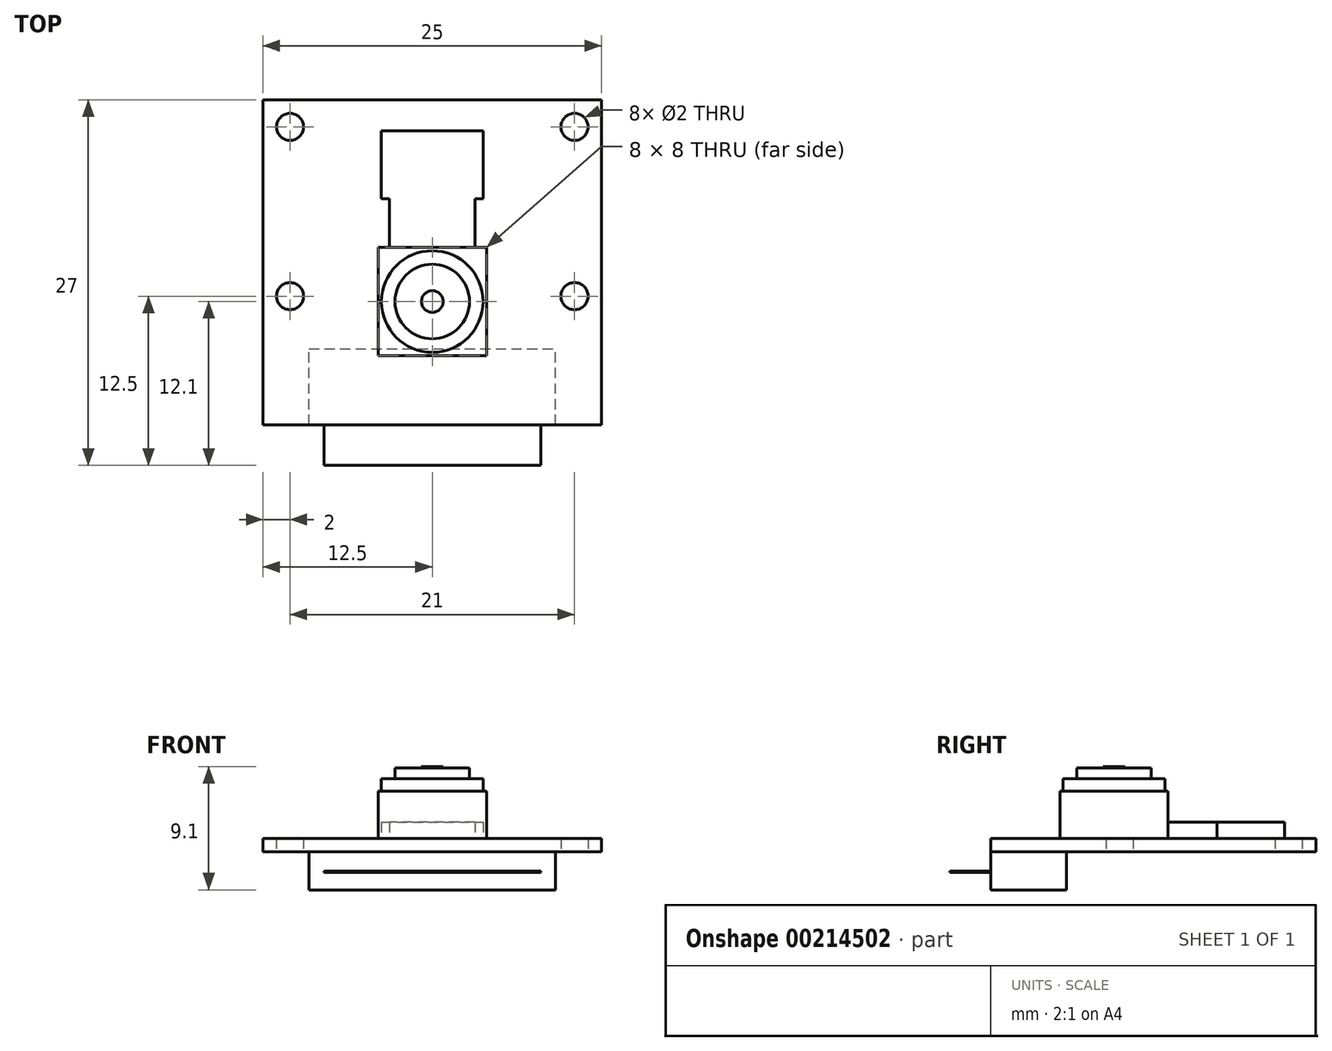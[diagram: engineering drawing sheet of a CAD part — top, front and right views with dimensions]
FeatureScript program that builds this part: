
annotation { "Feature Type Name" : "Feature", "Feature Type Description" : "" }
export const myFeature = defineFeature(function(context is Context, id is Id, definition is map)
    precondition{}
    {
        {
            var Q0;
            Q0=qCreatedBy(makeId("Top.planeOp"),FACE);
            var sketch = newSketch(context, id + "F0", { "sketchPlane" : qUnion([Q0])});
            skLineSegment(sketch, "E0.rect.bottom", {"start": v(12.5, 12) * mm, "end": v(-12.5, 12) * mm});
            skLineSegment(sketch, "E0.rect.top", {"start": v(12.5, -12) * mm, "end": v(-12.5, -12) * mm});
            skLineSegment(sketch, "E0.rect.left", {"start": v(12.5, 12) * mm, "end": v(12.5, -12) * mm});
            skLineSegment(sketch, "E0.rect.right", {"start": v(-12.5, 12) * mm, "end": v(-12.5, -12) * mm});
            skPoint(sketch, "E0.rect.middle", {"position": v(0, 0) * mm});
            skCircle(sketch, "E1", {"center": v(-10.5, 10) * mm, "radius": 1 * mm});
            skCircle(sketch, "E2", {"center": v(-10.5, -2.5) * mm, "radius": 1 * mm});
            skLineSegment(sketch, "E3", {"start": v(-10.5, 10) * mm, "end": v(-10.5, -12) * mm, "construction": true});
            skCircle(sketch, "E4.MirrorC", {"center": v(10.5, 10) * mm, "radius": 1 * mm});
            skCircle(sketch, "E5.MirrorC", {"center": v(10.5, -2.5) * mm, "radius": 1 * mm});
            skSolve(sketch);
        }
        {
            var Q0;
            Q0=makeQuery(id+"F0.imprint","IMPRINT",FACE,{"disambiguationData":[TD([[makeQuery(id+"F0.imprint","IMPRINT",EDGE,{"derivedFrom":sQuery(id+"F0.wireOp",EDGE,"E0.rect.bottom")}),1.0]])]});
            extrude(context, id + "F1", {"entities" : qUnion([Q0]), "depth" : 1 * mm});
        }
        {
            var Q0;
            Q0=makeQuery(id+"F1.opExtrude","CAP_FACE",FACE,{"disambiguationData":[OSD([sQuery(id+"F0.wireOp",EDGE,"E0.rect.bottom"),sQuery(id+"F0.wireOp",EDGE,"E0.rect.top"),sQuery(id+"F0.wireOp",EDGE,"E0.rect.left"),sQuery(id+"F0.wireOp",EDGE,"E0.rect.right"),sQuery(id+"F0.wireOp",EDGE,"E1"),sQuery(id+"F0.wireOp",EDGE,"E2"),sQuery(id+"F0.wireOp",EDGE,"E4.MirrorC"),sQuery(id+"F0.wireOp",EDGE,"E5.MirrorC")])],"isStart":false});
            var sketch = newSketch(context, id + "F2", { "sketchPlane" : qUnion([Q0])});
            skLineSegment(sketch, "E6", {"start": v(-12.5, -2.9) * mm, "end": v(12.5, -2.9) * mm, "construction": true});
            skLineSegment(sketch, "E7.rect.bottom", {"start": v(4, 1.1) * mm, "end": v(-4, 1.1) * mm});
            skLineSegment(sketch, "E7.rect.top", {"start": v(4, -6.9) * mm, "end": v(-4, -6.9) * mm});
            skLineSegment(sketch, "E7.rect.left", {"start": v(4, 1.1) * mm, "end": v(4, -6.9) * mm});
            skLineSegment(sketch, "E7.rect.right", {"start": v(-4, 1.1) * mm, "end": v(-4, -6.9) * mm});
            skPoint(sketch, "E7.rect.middle", {"position": v(0, -2.9) * mm});
            skCircle(sketch, "E8", {"center": v(0, -2.9) * mm, "radius": 3.75 * mm});
            skCircle(sketch, "E9", {"center": v(0, -2.9) * mm, "radius": 2.75 * mm});
            skLineSegment(sketch, "E10.bottom", {"start": v(-3.4, 1.1) * mm, "end": v(3.4, 1.1) * mm});
            skSolve(sketch);
        }
        {
            var Q0;
            Q0=qSketchRegion(id+"F2",true);
            var Q1;
            Q1=makeQuery(id+"F2.imprint","IMPRINT",FACE,{"disambiguationData":[TD([[makeQuery(id+"F2.imprint","IMPRINT",EDGE,{"derivedFrom":sQuery(id+"F2.wireOp",EDGE,"E8")}),1.0]])]});
            var Q2;
            Q2=makeQuery(id+"F2.imprint","IMPRINT",FACE,{"disambiguationData":[TD([[makeQuery(id+"F2.imprint","IMPRINT",EDGE,{"derivedFrom":sQuery(id+"F2.wireOp",EDGE,"E9")}),1.0]])]});
            extrude(context, id + "F3", {"entities" : qUnion([Q0, Q1, Q2]), "depth" : 3.5 * mm});
        }
        {
            var Q0;
            Q0=makeQuery(id+"F2.imprint","IMPRINT",FACE,{"disambiguationData":[TD([[makeQuery(id+"F2.imprint","IMPRINT",EDGE,{"derivedFrom":sQuery(id+"F2.wireOp",EDGE,"E8")}),1.0]])]});
            var Q1;
            Q1=makeQuery(id+"F2.imprint","IMPRINT",FACE,{"disambiguationData":[TD([[makeQuery(id+"F2.imprint","IMPRINT",EDGE,{"derivedFrom":sQuery(id+"F2.wireOp",EDGE,"E9")}),1.0]])]});
            extrude(context, id + "F4", {"entities" : qUnion([Q0, Q1]), "operationType" : NewBodyOperationType.ADD, "depth" : (3.5 + 0.9) * mm});
        }
        {
            var Q0;
            Q0=makeQuery(id+"F2.imprint","IMPRINT",FACE,{"disambiguationData":[TD([[makeQuery(id+"F2.imprint","IMPRINT",EDGE,{"derivedFrom":sQuery(id+"F2.wireOp",EDGE,"E9")}),1.0]])]});
            extrude(context, id + "F5", {"entities" : qUnion([Q0]), "operationType" : NewBodyOperationType.ADD, "depth" : 5.2 * mm});
        }
        {
            var Q0;
            Q0=makeQuery(id+"F5.opExtrude","CAP_FACE",FACE,{"disambiguationData":[OSD([sQuery(id+"F2.wireOp",EDGE,"E9")])],"isStart":false});
            var sketch = newSketch(context, id + "F6", { "sketchPlane" : qUnion([Q0])});
            skCircle(sketch, "E11", {"center": v(0, -2.9) * mm, "radius": 0.8 * mm});
            skSolve(sketch);
        }
        {
            var Q0;
            Q0=makeQuery(id+"F6.imprint","IMPRINT",FACE,{"disambiguationData":[TD([[makeQuery(id+"F6.imprint","IMPRINT",EDGE,{"derivedFrom":sQuery(id+"F6.wireOp",EDGE,"E11")}),1.0]])]});
            extrude(context, id + "F7", {"entities" : qUnion([Q0]), "depth" : 0.1 * mm});
        }
        {
            var Q0;
            Q0=makeQuery(id+"F1.opExtrude","CAP_FACE",FACE,{"disambiguationData":[OSD([sQuery(id+"F0.wireOp",EDGE,"E0.rect.bottom"),sQuery(id+"F0.wireOp",EDGE,"E0.rect.top"),sQuery(id+"F0.wireOp",EDGE,"E0.rect.left"),sQuery(id+"F0.wireOp",EDGE,"E0.rect.right"),sQuery(id+"F0.wireOp",EDGE,"E1"),sQuery(id+"F0.wireOp",EDGE,"E2"),sQuery(id+"F0.wireOp",EDGE,"E4.MirrorC"),sQuery(id+"F0.wireOp",EDGE,"E5.MirrorC")])],"isStart":true});
            var sketch = newSketch(context, id + "F8", { "sketchPlane" : qUnion([Q0])});
            skLineSegment(sketch, "E12.bottom", {"start": v(-9.1, 12) * mm, "end": v(9.1, 12) * mm});
            skLineSegment(sketch, "E12.top", {"start": v(-9.1, 6.4) * mm, "end": v(9.1, 6.4) * mm});
            skLineSegment(sketch, "E12.left", {"start": v(-9.1, 12) * mm, "end": v(-9.1, 6.4) * mm});
            skLineSegment(sketch, "E12.right", {"start": v(9.1, 12) * mm, "end": v(9.1, 6.4) * mm});
            skSolve(sketch);
        }
        {
            var Q0;
            Q0=qSketchRegion(id+"F8",true);
            extrude(context, id + "F9", {"entities" : qUnion([Q0]), "depth" : 2.8 * mm});
        }
        {
            var Q0;
            Q0=makeQuery(id+"F2.imprint","IMPRINT",FACE,{"disambiguationData":[TD([[makeQuery(id+"F2.imprint","IMPRINT",EDGE,{"derivedFrom":sQuery(id+"F2.wireOp",EDGE,"E7.rect.top")}),1.0]])]});
            var sketch = newSketch(context, id + "F10", { "sketchPlane" : qUnion([Q0])});
            skLineSegment(sketch, "E13.bottom", {"start": v(-3.75, 1.1) * mm, "end": v(3.75, 1.1) * mm});
            skLineSegment(sketch, "E13.top", {"start": v(-3.75, 9.7) * mm, "end": v(3.75, 9.7) * mm});
            skLineSegment(sketch, "E13.left", {"start": v(-3.75, 4.7) * mm, "end": v(-3.75, 9.7) * mm});
            skLineSegment(sketch, "E13.right", {"start": v(3.75, 4.7) * mm, "end": v(3.75, 9.7) * mm});
            skLineSegment(sketch, "E14", {"start": v(-3.75, 4.7) * mm, "end": v(-3.15, 4.7) * mm});
            skLineSegment(sketch, "E15", {"start": v(-3.15, 4.7) * mm, "end": v(-3.15, 1.1) * mm});
            skLineSegment(sketch, "E16", {"start": v(3.15, 4.7) * mm, "end": v(3.15, 1.1) * mm});
            skLineSegment(sketch, "E17.trimOffspring", {"start": v(3.15, 4.7) * mm, "end": v(3.75, 4.7) * mm});
            skSolve(sketch);
        }
        {
            var Q0;
            Q0=qSketchRegion(id+"F10",true);
            extrude(context, id + "F11", {"entities" : qUnion([Q0]), "depth" : 1.2 * mm});
        }
        {
            var Q0;
            Q0=makeQuery(id+"F1.opExtrude","CAP_FACE",FACE,{"disambiguationData":[OSD([sQuery(id+"F0.wireOp",EDGE,"E0.rect.bottom"),sQuery(id+"F0.wireOp",EDGE,"E0.rect.top"),sQuery(id+"F0.wireOp",EDGE,"E0.rect.left"),sQuery(id+"F0.wireOp",EDGE,"E0.rect.right"),sQuery(id+"F0.wireOp",EDGE,"E1"),sQuery(id+"F0.wireOp",EDGE,"E2"),sQuery(id+"F0.wireOp",EDGE,"E4.MirrorC"),sQuery(id+"F0.wireOp",EDGE,"E5.MirrorC")])],"isStart":true});
            cPlane(context, id + "F12", {"entities" : qUnion([Q0]), "cplaneType" : CPlaneType.OFFSET, "offset" : (2.8 / 2) * mm, "width" : 150 * mm, "height" : 150 * mm});
        }
        {
            var Q0;
            Q0=qCreatedBy(id+"F12.planeOp",FACE);
            var sketch = newSketch(context, id + "F13", { "sketchPlane" : qUnion([Q0])});
            skLineSegment(sketch, "E18.bottom", {"start": v(-8, 12) * mm, "end": v(8, 12) * mm});
            skLineSegment(sketch, "E18.top", {"start": v(-8, 15) * mm, "end": v(8, 15) * mm});
            skLineSegment(sketch, "E18.left", {"start": v(-8, 12) * mm, "end": v(-8, 15) * mm});
            skLineSegment(sketch, "E18.right", {"start": v(8, 12) * mm, "end": v(8, 15) * mm});
            skSolve(sketch);
        }
        {
            var Q0;
            Q0=makeQuery(id+"F13.imprint","IMPRINT",FACE,{"disambiguationData":[TD([[makeQuery(id+"F13.imprint","IMPRINT",EDGE,{"derivedFrom":sQuery(id+"F13.wireOp",EDGE,"E18.bottom")}),1.0]])]});
            extrude(context, id + "F14", {"entities" : qUnion([Q0]), "depth" : 0.1 * mm});
        }
        {
            var Q0;
            Q0=makeQuery(id+"F1.opExtrude","SWEPT_BODY",BODY,{"disambiguationData":[OSD([sQuery(id+"F0.wireOp",EDGE,"E0.rect.bottom"),sQuery(id+"F0.wireOp",EDGE,"E0.rect.top"),sQuery(id+"F0.wireOp",EDGE,"E0.rect.left"),sQuery(id+"F0.wireOp",EDGE,"E0.rect.right"),sQuery(id+"F0.wireOp",EDGE,"E1"),sQuery(id+"F0.wireOp",EDGE,"E2"),sQuery(id+"F0.wireOp",EDGE,"E4.MirrorC"),sQuery(id+"F0.wireOp",EDGE,"E5.MirrorC")])]});
            transform(context, id + "F15", {"entities" : qUnion([Q0]), "transformType" : TransformType.TRANSLATION_3D, "dx" : 0 * mm, "dy" : 0 * mm, "dz" : 0 * mm, "makeCopy" : true});
        }
    });
